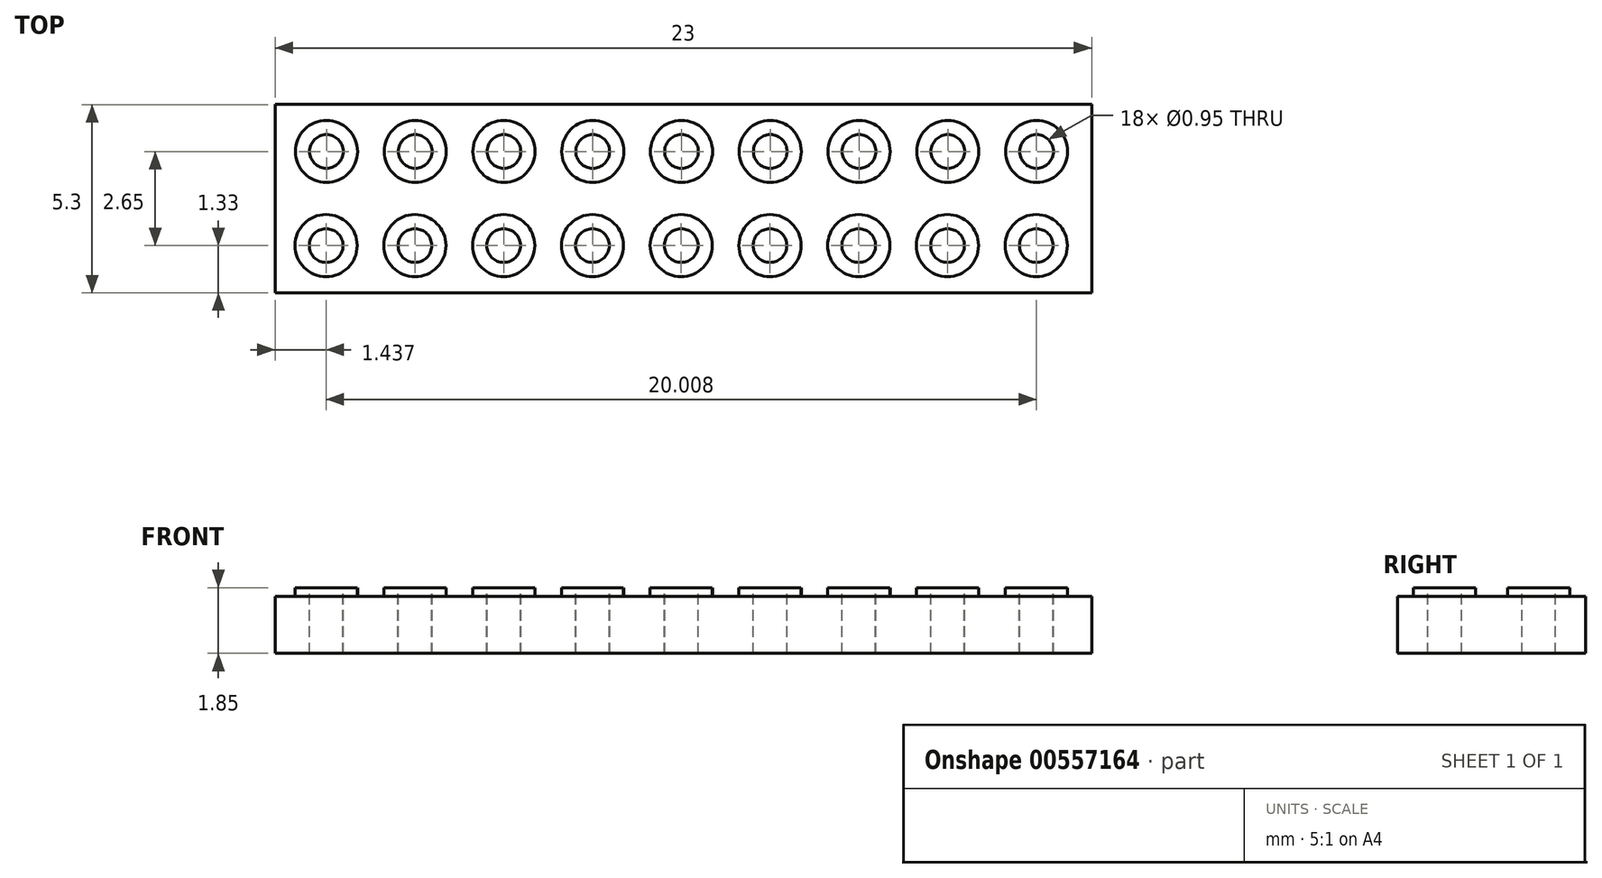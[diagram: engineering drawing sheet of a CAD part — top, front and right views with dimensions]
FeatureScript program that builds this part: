
annotation { "Feature Type Name" : "Feature", "Feature Type Description" : "" }
export const myFeature = defineFeature(function(context is Context, id is Id, definition is map)
    precondition{}
    {
        {
            var Q0;
            Q0=qCreatedBy(makeId("Top.planeOp"),FACE);
            var sketch = newSketch(context, id + "F0", { "sketchPlane" : qUnion([Q0])});
            skLineSegment(sketch, "E0.bottom", {"start": v(-28.71, 40.12) * mm, "end": v(-5.71, 40.12) * mm});
            skLineSegment(sketch, "E0.top", {"start": v(-28.71, 34.82) * mm, "end": v(-5.71, 34.82) * mm});
            skLineSegment(sketch, "E1", {"start": v(-28.71, 37.47) * mm, "end": v(-5.71, 37.47) * mm, "construction": true});
            skPoint(sketch, "E2", {"position": v(-28.71, 37.47) * mm});
            skPoint(sketch, "E3", {"position": v(-5.71, 37.47) * mm});
            skLineSegment(sketch, "E4", {"start": v(-28.71, 40.12) * mm, "end": v(-28.71, 37.47) * mm});
            skLineSegment(sketch, "E5", {"start": v(-28.71, 34.82) * mm, "end": v(-28.71, 37.47) * mm});
            skLineSegment(sketch, "E6", {"start": v(-5.71, 34.82) * mm, "end": v(-5.71, 37.47) * mm});
            skLineSegment(sketch, "E7", {"start": v(-5.71, 40.12) * mm, "end": v(-5.71, 37.47) * mm});
            skLineSegment(sketch, "E8", {"start": v(-28.71, 38.8) * mm, "end": v(-5.71, 38.8) * mm, "construction": true});
            skLineSegment(sketch, "E9", {"start": v(-5.71, 36.15) * mm, "end": v(-28.71, 36.15) * mm, "construction": true});
            skCircle(sketch, "E10", {"center": v(-27.26, 38.8) * mm, "radius": 0.47 * mm});
            skCircle(sketch, "E11", {"center": v(-27.26, 38.8) * mm, "radius": 0.88 * mm});
            skCircle(sketch, "E12.1.0.0", {"center": v(-24.76, 38.8) * mm, "radius": 0.47 * mm});
            skCircle(sketch, "E12.1.0.1", {"center": v(-24.76, 38.8) * mm, "radius": 0.88 * mm});
            skCircle(sketch, "E12.2.0.0", {"center": v(-22.26, 38.8) * mm, "radius": 0.47 * mm});
            skCircle(sketch, "E12.2.0.1", {"center": v(-22.26, 38.8) * mm, "radius": 0.88 * mm});
            skCircle(sketch, "E12.3.0.0", {"center": v(-19.76, 38.8) * mm, "radius": 0.47 * mm});
            skCircle(sketch, "E12.3.0.1", {"center": v(-19.76, 38.8) * mm, "radius": 0.88 * mm});
            skCircle(sketch, "E12.4.0.0", {"center": v(-17.26, 38.8) * mm, "radius": 0.47 * mm});
            skCircle(sketch, "E12.4.0.1", {"center": v(-17.26, 38.8) * mm, "radius": 0.88 * mm});
            skCircle(sketch, "E12.5.0.0", {"center": v(-14.76, 38.8) * mm, "radius": 0.47 * mm});
            skCircle(sketch, "E12.5.0.1", {"center": v(-14.76, 38.8) * mm, "radius": 0.88 * mm});
            skCircle(sketch, "E12.6.0.0", {"center": v(-12.26, 38.8) * mm, "radius": 0.47 * mm});
            skCircle(sketch, "E12.6.0.1", {"center": v(-12.26, 38.8) * mm, "radius": 0.88 * mm});
            skCircle(sketch, "E12.7.0.0", {"center": v(-9.76, 38.8) * mm, "radius": 0.47 * mm});
            skCircle(sketch, "E12.7.0.1", {"center": v(-9.76, 38.8) * mm, "radius": 0.88 * mm});
            skCircle(sketch, "E12.8.0.0", {"center": v(-7.26, 38.8) * mm, "radius": 0.47 * mm});
            skCircle(sketch, "E12.8.0.1", {"center": v(-7.26, 38.8) * mm, "radius": 0.88 * mm});
            skLineSegment(sketch, "E12.direction1", {"start": v(-27.26, 38.8) * mm, "end": v(-24.76, 38.8) * mm, "construction": true});
            skCircle(sketch, "E13", {"center": v(-27.27, 36.15) * mm, "radius": 0.47 * mm});
            skCircle(sketch, "E14", {"center": v(-27.27, 36.15) * mm, "radius": 0.88 * mm});
            skCircle(sketch, "E15.1.0.0", {"center": v(-24.77, 36.15) * mm, "radius": 0.47 * mm});
            skCircle(sketch, "E15.1.0.1", {"center": v(-24.77, 36.15) * mm, "radius": 0.88 * mm});
            skCircle(sketch, "E15.2.0.0", {"center": v(-22.27, 36.15) * mm, "radius": 0.47 * mm});
            skCircle(sketch, "E15.2.0.1", {"center": v(-22.27, 36.15) * mm, "radius": 0.88 * mm});
            skCircle(sketch, "E15.3.0.0", {"center": v(-19.77, 36.15) * mm, "radius": 0.47 * mm});
            skCircle(sketch, "E15.3.0.1", {"center": v(-19.77, 36.15) * mm, "radius": 0.88 * mm});
            skCircle(sketch, "E15.4.0.0", {"center": v(-17.27, 36.15) * mm, "radius": 0.47 * mm});
            skCircle(sketch, "E15.4.0.1", {"center": v(-17.27, 36.15) * mm, "radius": 0.88 * mm});
            skCircle(sketch, "E15.5.0.0", {"center": v(-14.77, 36.15) * mm, "radius": 0.47 * mm});
            skCircle(sketch, "E15.5.0.1", {"center": v(-14.77, 36.15) * mm, "radius": 0.88 * mm});
            skCircle(sketch, "E15.6.0.0", {"center": v(-12.27, 36.15) * mm, "radius": 0.47 * mm});
            skCircle(sketch, "E15.6.0.1", {"center": v(-12.27, 36.15) * mm, "radius": 0.88 * mm});
            skCircle(sketch, "E15.7.0.0", {"center": v(-9.77, 36.15) * mm, "radius": 0.47 * mm});
            skCircle(sketch, "E15.7.0.1", {"center": v(-9.77, 36.15) * mm, "radius": 0.88 * mm});
            skCircle(sketch, "E15.8.0.0", {"center": v(-7.27, 36.15) * mm, "radius": 0.47 * mm});
            skCircle(sketch, "E15.8.0.1", {"center": v(-7.27, 36.15) * mm, "radius": 0.88 * mm});
            skSolve(sketch);
        }
        {
            var Q0;
            Q0=makeQuery(id+"F0.imprint","IMPRINT",FACE,{"disambiguationData":[TD([[makeQuery(id+"F0.imprint","IMPRINT",EDGE,{"derivedFrom":sQuery(id+"F0.wireOp",EDGE,"E0.bottom")}),-1.0]])]});
            var Q1;
            Q1=makeQuery(id+"F0.imprint","IMPRINT",FACE,{"disambiguationData":[TD([[makeQuery(id+"F0.imprint","IMPRINT",EDGE,{"derivedFrom":sQuery(id+"F0.wireOp",EDGE,"E10")}),-1.0]])]});
            var Q2;
            Q2=makeQuery(id+"F0.imprint","IMPRINT",FACE,{"disambiguationData":[TD([[makeQuery(id+"F0.imprint","IMPRINT",EDGE,{"derivedFrom":sQuery(id+"F0.wireOp",EDGE,"E12.1.0.0")}),-1.0]])]});
            var Q3;
            Q3=makeQuery(id+"F0.imprint","IMPRINT",FACE,{"disambiguationData":[TD([[makeQuery(id+"F0.imprint","IMPRINT",EDGE,{"derivedFrom":sQuery(id+"F0.wireOp",EDGE,"E12.2.0.0")}),-1.0]])]});
            var Q4;
            Q4=makeQuery(id+"F0.imprint","IMPRINT",FACE,{"disambiguationData":[TD([[makeQuery(id+"F0.imprint","IMPRINT",EDGE,{"derivedFrom":sQuery(id+"F0.wireOp",EDGE,"E12.3.0.0")}),-1.0]])]});
            var Q5;
            Q5=makeQuery(id+"F0.imprint","IMPRINT",FACE,{"disambiguationData":[TD([[makeQuery(id+"F0.imprint","IMPRINT",EDGE,{"derivedFrom":sQuery(id+"F0.wireOp",EDGE,"E12.4.0.0")}),-1.0]])]});
            var Q6;
            Q6=makeQuery(id+"F0.imprint","IMPRINT",FACE,{"disambiguationData":[TD([[makeQuery(id+"F0.imprint","IMPRINT",EDGE,{"derivedFrom":sQuery(id+"F0.wireOp",EDGE,"E12.5.0.0")}),-1.0]])]});
            var Q7;
            Q7=makeQuery(id+"F0.imprint","IMPRINT",FACE,{"disambiguationData":[TD([[makeQuery(id+"F0.imprint","IMPRINT",EDGE,{"derivedFrom":sQuery(id+"F0.wireOp",EDGE,"E12.6.0.0")}),-1.0]])]});
            var Q8;
            Q8=makeQuery(id+"F0.imprint","IMPRINT",FACE,{"disambiguationData":[TD([[makeQuery(id+"F0.imprint","IMPRINT",EDGE,{"derivedFrom":sQuery(id+"F0.wireOp",EDGE,"E12.7.0.0")}),-1.0]])]});
            var Q9;
            Q9=makeQuery(id+"F0.imprint","IMPRINT",FACE,{"disambiguationData":[TD([[makeQuery(id+"F0.imprint","IMPRINT",EDGE,{"derivedFrom":sQuery(id+"F0.wireOp",EDGE,"E12.8.0.0")}),-1.0]])]});
            var Q10;
            Q10=makeQuery(id+"F0.imprint","IMPRINT",FACE,{"disambiguationData":[TD([[makeQuery(id+"F0.imprint","IMPRINT",EDGE,{"derivedFrom":sQuery(id+"F0.wireOp",EDGE,"E15.8.0.0")}),-1.0]])]});
            var Q11;
            Q11=makeQuery(id+"F0.imprint","IMPRINT",FACE,{"disambiguationData":[TD([[makeQuery(id+"F0.imprint","IMPRINT",EDGE,{"derivedFrom":sQuery(id+"F0.wireOp",EDGE,"E15.7.0.0")}),-1.0]])]});
            var Q12;
            Q12=makeQuery(id+"F0.imprint","IMPRINT",FACE,{"disambiguationData":[TD([[makeQuery(id+"F0.imprint","IMPRINT",EDGE,{"derivedFrom":sQuery(id+"F0.wireOp",EDGE,"E15.6.0.0")}),-1.0]])]});
            var Q13;
            Q13=makeQuery(id+"F0.imprint","IMPRINT",FACE,{"disambiguationData":[TD([[makeQuery(id+"F0.imprint","IMPRINT",EDGE,{"derivedFrom":sQuery(id+"F0.wireOp",EDGE,"E15.5.0.0")}),-1.0]])]});
            var Q14;
            Q14=makeQuery(id+"F0.imprint","IMPRINT",FACE,{"disambiguationData":[TD([[makeQuery(id+"F0.imprint","IMPRINT",EDGE,{"derivedFrom":sQuery(id+"F0.wireOp",EDGE,"E15.4.0.0")}),-1.0]])]});
            var Q15;
            Q15=makeQuery(id+"F0.imprint","IMPRINT",FACE,{"disambiguationData":[TD([[makeQuery(id+"F0.imprint","IMPRINT",EDGE,{"derivedFrom":sQuery(id+"F0.wireOp",EDGE,"E15.3.0.0")}),-1.0]])]});
            var Q16;
            Q16=makeQuery(id+"F0.imprint","IMPRINT",FACE,{"disambiguationData":[TD([[makeQuery(id+"F0.imprint","IMPRINT",EDGE,{"derivedFrom":sQuery(id+"F0.wireOp",EDGE,"E15.2.0.0")}),-1.0]])]});
            var Q17;
            Q17=makeQuery(id+"F0.imprint","IMPRINT",FACE,{"disambiguationData":[TD([[makeQuery(id+"F0.imprint","IMPRINT",EDGE,{"derivedFrom":sQuery(id+"F0.wireOp",EDGE,"E15.1.0.0")}),-1.0]])]});
            var Q18;
            Q18=makeQuery(id+"F0.imprint","IMPRINT",FACE,{"disambiguationData":[TD([[makeQuery(id+"F0.imprint","IMPRINT",EDGE,{"derivedFrom":sQuery(id+"F0.wireOp",EDGE,"E13")}),-1.0]])]});
            extrude(context, id + "F1", {"entities" : qUnion([Q0, Q1, Q2, Q3, Q4, Q5, Q6, Q7, Q8, Q9, Q10, Q11, Q12, Q13, Q14, Q15, Q16, Q17, Q18]), "oppositeDirection" : true, "depth" : 1.6 * mm, "offsetDistance" : 25 * mm});
        }
        {
            var Q0;
            Q0=makeQuery(id+"F0.imprint","IMPRINT",FACE,{"disambiguationData":[TD([[makeQuery(id+"F0.imprint","IMPRINT",EDGE,{"derivedFrom":sQuery(id+"F0.wireOp",EDGE,"E10")}),-1.0]])]});
            var Q1;
            Q1=makeQuery(id+"F0.imprint","IMPRINT",FACE,{"disambiguationData":[TD([[makeQuery(id+"F0.imprint","IMPRINT",EDGE,{"derivedFrom":sQuery(id+"F0.wireOp",EDGE,"E12.1.0.0")}),-1.0]])]});
            var Q2;
            Q2=makeQuery(id+"F0.imprint","IMPRINT",FACE,{"disambiguationData":[TD([[makeQuery(id+"F0.imprint","IMPRINT",EDGE,{"derivedFrom":sQuery(id+"F0.wireOp",EDGE,"E12.2.0.0")}),-1.0]])]});
            var Q3;
            Q3=makeQuery(id+"F0.imprint","IMPRINT",FACE,{"disambiguationData":[TD([[makeQuery(id+"F0.imprint","IMPRINT",EDGE,{"derivedFrom":sQuery(id+"F0.wireOp",EDGE,"E12.3.0.0")}),-1.0]])]});
            var Q4;
            Q4=makeQuery(id+"F0.imprint","IMPRINT",FACE,{"disambiguationData":[TD([[makeQuery(id+"F0.imprint","IMPRINT",EDGE,{"derivedFrom":sQuery(id+"F0.wireOp",EDGE,"E12.4.0.0")}),-1.0]])]});
            var Q5;
            Q5=makeQuery(id+"F0.imprint","IMPRINT",FACE,{"disambiguationData":[TD([[makeQuery(id+"F0.imprint","IMPRINT",EDGE,{"derivedFrom":sQuery(id+"F0.wireOp",EDGE,"E12.5.0.0")}),-1.0]])]});
            var Q6;
            Q6=makeQuery(id+"F0.imprint","IMPRINT",FACE,{"disambiguationData":[TD([[makeQuery(id+"F0.imprint","IMPRINT",EDGE,{"derivedFrom":sQuery(id+"F0.wireOp",EDGE,"E12.6.0.0")}),-1.0]])]});
            var Q7;
            Q7=makeQuery(id+"F0.imprint","IMPRINT",FACE,{"disambiguationData":[TD([[makeQuery(id+"F0.imprint","IMPRINT",EDGE,{"derivedFrom":sQuery(id+"F0.wireOp",EDGE,"E12.7.0.0")}),-1.0]])]});
            var Q8;
            Q8=makeQuery(id+"F0.imprint","IMPRINT",FACE,{"disambiguationData":[TD([[makeQuery(id+"F0.imprint","IMPRINT",EDGE,{"derivedFrom":sQuery(id+"F0.wireOp",EDGE,"E13")}),-1.0]])]});
            var Q9;
            Q9=makeQuery(id+"F0.imprint","IMPRINT",FACE,{"disambiguationData":[TD([[makeQuery(id+"F0.imprint","IMPRINT",EDGE,{"derivedFrom":sQuery(id+"F0.wireOp",EDGE,"E15.1.0.0")}),-1.0]])]});
            var Q10;
            Q10=makeQuery(id+"F0.imprint","IMPRINT",FACE,{"disambiguationData":[TD([[makeQuery(id+"F0.imprint","IMPRINT",EDGE,{"derivedFrom":sQuery(id+"F0.wireOp",EDGE,"E15.2.0.0")}),-1.0]])]});
            var Q11;
            Q11=makeQuery(id+"F0.imprint","IMPRINT",FACE,{"disambiguationData":[TD([[makeQuery(id+"F0.imprint","IMPRINT",EDGE,{"derivedFrom":sQuery(id+"F0.wireOp",EDGE,"E15.3.0.0")}),-1.0]])]});
            var Q12;
            Q12=makeQuery(id+"F0.imprint","IMPRINT",FACE,{"disambiguationData":[TD([[makeQuery(id+"F0.imprint","IMPRINT",EDGE,{"derivedFrom":sQuery(id+"F0.wireOp",EDGE,"E15.4.0.0")}),-1.0]])]});
            var Q13;
            Q13=makeQuery(id+"F0.imprint","IMPRINT",FACE,{"disambiguationData":[TD([[makeQuery(id+"F0.imprint","IMPRINT",EDGE,{"derivedFrom":sQuery(id+"F0.wireOp",EDGE,"E15.5.0.0")}),-1.0]])]});
            var Q14;
            Q14=makeQuery(id+"F0.imprint","IMPRINT",FACE,{"disambiguationData":[TD([[makeQuery(id+"F0.imprint","IMPRINT",EDGE,{"derivedFrom":sQuery(id+"F0.wireOp",EDGE,"E15.6.0.0")}),-1.0]])]});
            var Q15;
            Q15=makeQuery(id+"F0.imprint","IMPRINT",FACE,{"disambiguationData":[TD([[makeQuery(id+"F0.imprint","IMPRINT",EDGE,{"derivedFrom":sQuery(id+"F0.wireOp",EDGE,"E15.7.0.0")}),-1.0]])]});
            var Q16;
            Q16=makeQuery(id+"F0.imprint","IMPRINT",FACE,{"disambiguationData":[TD([[makeQuery(id+"F0.imprint","IMPRINT",EDGE,{"derivedFrom":sQuery(id+"F0.wireOp",EDGE,"E15.8.0.0")}),-1.0]])]});
            var Q17;
            Q17=makeQuery(id+"F0.imprint","IMPRINT",FACE,{"disambiguationData":[TD([[makeQuery(id+"F0.imprint","IMPRINT",EDGE,{"derivedFrom":sQuery(id+"F0.wireOp",EDGE,"E12.8.0.0")}),-1.0]])]});
            extrude(context, id + "F2", {"entities" : qUnion([Q0, Q1, Q2, Q3, Q4, Q5, Q6, Q7, Q8, Q9, Q10, Q11, Q12, Q13, Q14, Q15, Q16, Q17]), "operationType" : NewBodyOperationType.ADD, "depth" : .25 * mm, "offsetDistance" : 25 * mm});
        }
    });
